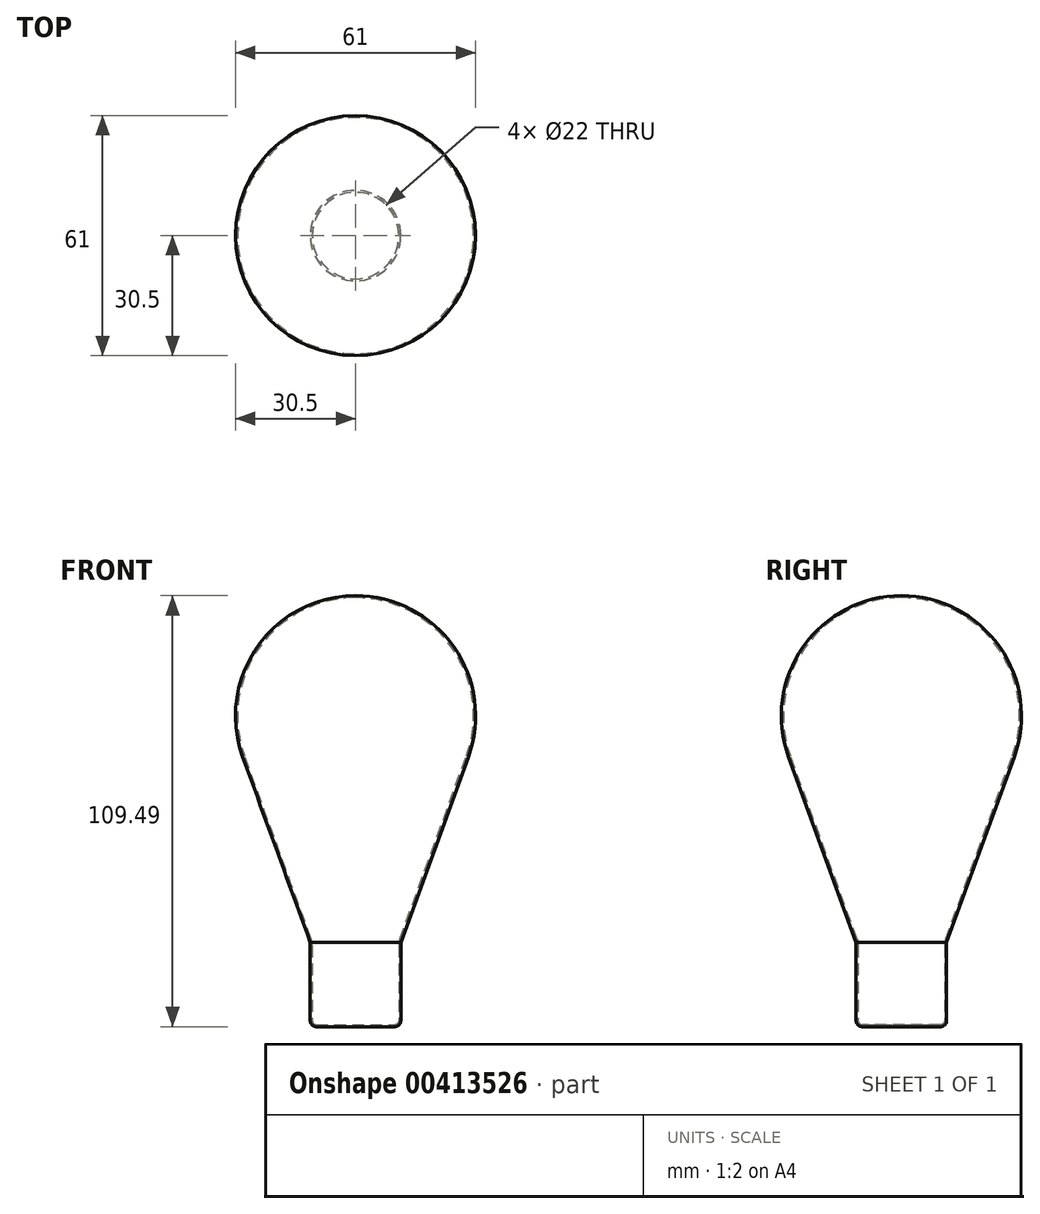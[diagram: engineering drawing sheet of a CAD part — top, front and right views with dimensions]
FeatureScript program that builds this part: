
annotation { "Feature Type Name" : "Feature", "Feature Type Description" : "" }
export const myFeature = defineFeature(function(context is Context, id is Id, definition is map)
    precondition{}
    {
        {
            var Q0;
            Q0=qCreatedBy(makeId("Front.planeOp"),FACE);
            var sketch = newSketch(context, id + "F0", { "sketchPlane" : qUnion([Q0])});
            skArc(sketch, "E0", {"start": v(0, 87.5) * mm, "mid": v(-24.57, 74.7) * mm, "end": v(-28.2, 47.23) * mm});
            skLineSegment(sketch, "E1", {"start": v(0, 0) * mm, "end": v(0, -0.5) * mm});
            skLineSegment(sketch, "E2", {"start": v(-11.3, 0.83) * mm, "end": v(-28.2, 47.23) * mm});
            skLineSegment(sketch, "E3", {"start": v(-11, -0.88) * mm, "end": v(-11, -20) * mm});
            skLineSegment(sketch, "E4", {"start": v(-10, -21) * mm, "end": v(0, -21) * mm});
            skPoint(sketch, "E5.visualSharp", {"position": v(-11, -21) * mm});
            skArc(sketch, "E5.filletArc", {"start": v(-11, -20) * mm, "mid": v(-10.7, -20.7) * mm, "end": v(-10, -21) * mm});
            skPoint(sketch, "E6.visualSharp", {"position": v(-11, 0) * mm});
            skArc(sketch, "E6.filletArc", {"start": v(-11, -0.88) * mm, "mid": v(-11.08, -0.01) * mm, "end": v(-11.3, 0.83) * mm});
            skLineSegment(sketch, "E7.0", {"start": v(-10, -21.5) * mm, "end": v(0, -21.5) * mm});
            skArc(sketch, "E7.1", {"start": v(0, 88) * mm, "mid": v(-24.98, 74.99) * mm, "end": v(-28.66, 47.06) * mm});
            skLineSegment(sketch, "E7.2", {"start": v(-11.5, -0.09) * mm, "end": v(-28.66, 47.06) * mm});
            skLineSegment(sketch, "E7.3", {"start": v(-11.5, -0.09) * mm, "end": v(-11.5, -20) * mm});
            skArc(sketch, "E7.4", {"start": v(-11.5, -20) * mm, "mid": v(-11.06, -21.06) * mm, "end": v(-10, -21.5) * mm});
            skLineSegment(sketch, "E8", {"start": v(0, -21.5) * mm, "end": v(0, -21) * mm});
            skLineSegment(sketch, "E9", {"start": v(0, 88) * mm, "end": v(0, 87.5) * mm});
            skSolve(sketch);
        }
        {
            var Q0;
            Q0=qCreatedBy(makeId("Front.planeOp"),FACE);
            var sketch = newSketch(context, id + "F1", { "sketchPlane" : qUnion([Q0])});
            skLineSegment(sketch, "E10", {"start": v(0, 0) * mm, "end": v(0, 87) * mm, "construction": true});
            skSolve(sketch);
        }
        {
            var Q0;
            Q0=makeQuery(id+"F0.imprint","IMPRINT",FACE,{"disambiguationData":[TD([[makeQuery(id+"F0.imprint","IMPRINT",EDGE,{"derivedFrom":sQuery(id+"F0.wireOp",EDGE,"E0")}),-1.0]])]});
            var Q1;
            Q1=sQuery(id+"F1.wireOp",EDGE,"E10");
            revolve(context, id + "F2", {"entities" : qUnion([Q0]), "axis" : qUnion([Q1]), "revolveType" : RevolveType.FULL});
        }
    });
